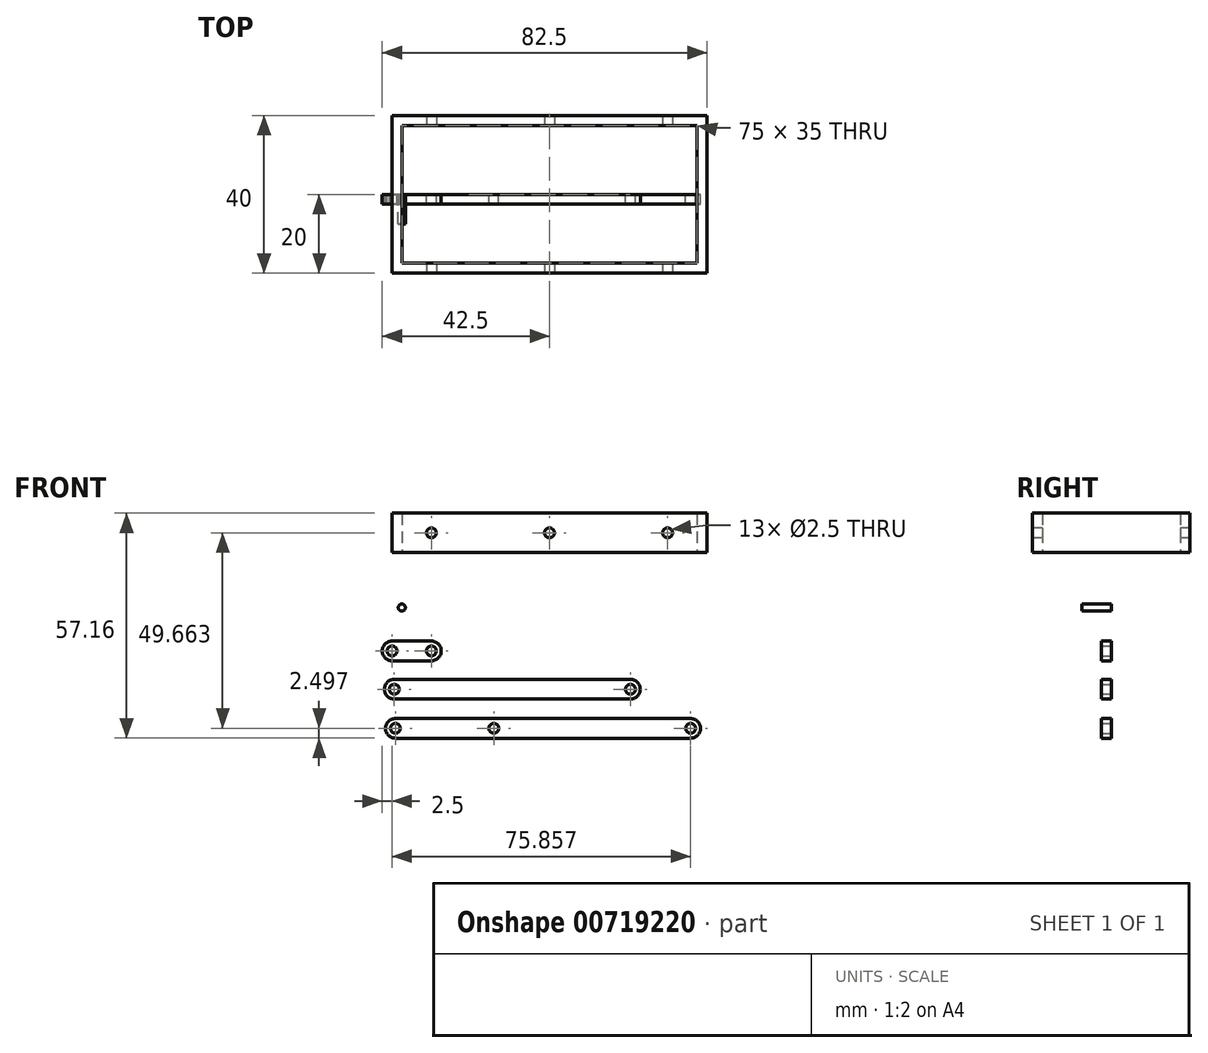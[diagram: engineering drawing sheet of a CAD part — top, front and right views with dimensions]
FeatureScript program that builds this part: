
annotation { "Feature Type Name" : "Feature", "Feature Type Description" : "" }
export const myFeature = defineFeature(function(context is Context, id is Id, definition is map)
    precondition{}
    {
        {
            assignVariable(context, id + "F0", {"name" : "thickness", "anyValue" : 2.5});
        }
        {
            var Q0;
            Q0=qCreatedBy(makeId("Front.planeOp"),FACE);
            var sketch = newSketch(context, id + "F1", { "sketchPlane" : qUnion([Q0])});
            skArc(sketch, "E0", {"start": v(0, 2.5) * mm, "mid": v(-2.5, 0) * mm, "end": v(0, -2.5) * mm});
            skArc(sketch, "E1", {"start": v(10, -2.5) * mm, "mid": v(12.5, 0) * mm, "end": v(10, 2.5) * mm});
            skLineSegment(sketch, "E2", {"start": v(0, 2.5) * mm, "end": v(10, 2.5) * mm});
            skLineSegment(sketch, "E3", {"start": v(0, -2.5) * mm, "end": v(10, -2.5) * mm});
            skCircle(sketch, "E4", {"center": v(0, 0) * mm, "radius": 1.25 * mm});
            skCircle(sketch, "E5", {"center": v(10, 0) * mm, "radius": 1.25 * mm});
            skSolve(sketch);
        }
        {
            var Q0;
            Q0=makeQuery(id+"F1.imprint","IMPRINT",FACE,{"disambiguationData":[TD([[makeQuery(id+"F1.imprint","IMPRINT",EDGE,{"derivedFrom":sQuery(id+"F1.wireOp",EDGE,"E0")}),1.0]])]});
            extrude(context, id + "F2", {"entities" : qUnion([Q0]), "depth" : (getVariable(context, 'thickness')) * mm, "offsetDistance" : 25 * mm});
        }
        {
            var Q0;
            Q0=qCreatedBy(makeId("Front.planeOp"),FACE);
            var sketch = newSketch(context, id + "F3", { "sketchPlane" : qUnion([Q0])});
            skArc(sketch, "E6", {"start": v(0.57, -7.23) * mm, "mid": v(-1.93, -9.73) * mm, "end": v(0.57, -12.23) * mm});
            skArc(sketch, "E7", {"start": v(60.57, -12.23) * mm, "mid": v(63.07, -9.73) * mm, "end": v(60.57, -7.23) * mm});
            skLineSegment(sketch, "E8", {"start": v(0.57, -7.23) * mm, "end": v(60.57, -7.23) * mm});
            skLineSegment(sketch, "E9", {"start": v(0.57, -12.23) * mm, "end": v(60.57, -12.23) * mm});
            skCircle(sketch, "E10", {"center": v(0.57, -9.73) * mm, "radius": 1.25 * mm});
            skCircle(sketch, "E11", {"center": v(60.57, -9.73) * mm, "radius": 1.25 * mm});
            skSolve(sketch);
        }
        {
            var Q0;
            Q0=makeQuery(id+"F3.imprint","IMPRINT",FACE,{"disambiguationData":[TD([[makeQuery(id+"F3.imprint","IMPRINT",EDGE,{"derivedFrom":sQuery(id+"F3.wireOp",EDGE,"E6")}),1.0]])]});
            extrude(context, id + "F4", {"entities" : qUnion([Q0]), "depth" : (getVariable(context, 'thickness')) * mm, "offsetDistance" : 25 * mm});
        }
        {
            var Q0;
            Q0=qCreatedBy(makeId("Front.planeOp"),FACE);
            var sketch = newSketch(context, id + "F5", { "sketchPlane" : qUnion([Q0])});
            skArc(sketch, "E12", {"start": v(0.86, -17.16) * mm, "mid": v(-1.64, -19.66) * mm, "end": v(0.86, -22.16) * mm});
            skArc(sketch, "E13", {"start": v(75.86, -22.16) * mm, "mid": v(78.36, -19.66) * mm, "end": v(75.86, -17.16) * mm});
            skLineSegment(sketch, "E14", {"start": v(0.86, -17.16) * mm, "end": v(75.86, -17.16) * mm});
            skLineSegment(sketch, "E15", {"start": v(0.86, -22.16) * mm, "end": v(75.86, -22.16) * mm});
            skCircle(sketch, "E16", {"center": v(0.86, -19.66) * mm, "radius": 1.25 * mm});
            skCircle(sketch, "E17", {"center": v(75.86, -19.66) * mm, "radius": 1.25 * mm});
            skCircle(sketch, "E18", {"center": v(25.86, -19.66) * mm, "radius": 1.25 * mm});
            skSolve(sketch);
        }
        {
            var Q0;
            Q0=makeQuery(id+"F5.imprint","IMPRINT",FACE,{"disambiguationData":[TD([[makeQuery(id+"F5.imprint","IMPRINT",EDGE,{"derivedFrom":sQuery(id+"F5.wireOp",EDGE,"E12")}),1.0]])]});
            extrude(context, id + "F6", {"entities" : qUnion([Q0]), "depth" : (getVariable(context, 'thickness')) * mm, "offsetDistance" : 25 * mm});
        }
        {
            var Q0;
            Q0=qCreatedBy(makeId("Top.planeOp"),FACE);
            cPlane(context, id + "F7", {"entities" : qUnion([Q0]), "cplaneType" : CPlaneType.OFFSET, "offset" : 25 * mm, "width" : 150 * mm, "height" : 150 * mm});
        }
        {
            var Q0;
            Q0=qCreatedBy(id+"F7.planeOp",FACE);
            var sketch = newSketch(context, id + "F8", { "sketchPlane" : qUnion([Q0])});
            skLineSegment(sketch, "E19.bottom", {"start": v(0, 20) * mm, "end": v(80, 20) * mm});
            skLineSegment(sketch, "E19.top", {"start": v(0, -20) * mm, "end": v(80, -20) * mm});
            skLineSegment(sketch, "E19.left", {"start": v(0, 20) * mm, "end": v(0, -20) * mm});
            skLineSegment(sketch, "E19.right", {"start": v(80, 20) * mm, "end": v(80, -20) * mm});
            skLineSegment(sketch, "E20.0", {"start": v(2.5, 17.5) * mm, "end": v(77.5, 17.5) * mm});
            skLineSegment(sketch, "E20.1", {"start": v(2.5, 17.5) * mm, "end": v(2.5, -17.5) * mm});
            skLineSegment(sketch, "E20.2", {"start": v(2.5, -17.5) * mm, "end": v(77.5, -17.5) * mm});
            skLineSegment(sketch, "E20.3", {"start": v(77.5, 17.5) * mm, "end": v(77.5, -17.5) * mm});
            skSolve(sketch);
        }
        {
            var Q0;
            Q0=makeQuery(id+"F8.imprint","IMPRINT",FACE,{"disambiguationData":[TD([[makeQuery(id+"F8.imprint","IMPRINT",EDGE,{"derivedFrom":sQuery(id+"F8.wireOp",EDGE,"E19.bottom")}),-1.0]])]});
            extrude(context, id + "F9", {"entities" : qUnion([Q0]), "depth" : 10 * mm, "offsetDistance" : 25 * mm});
        }
        {
            var Q0;
            Q0=makeQuery(id+"F9.opExtrude","SWEPT_FACE",FACE,{"disambiguationData":[OSD([sQuery(id+"F8.wireOp",EDGE,"E19.top")])]});
            var sketch = newSketch(context, id + "F10", { "sketchPlane" : qUnion([Q0])});
            skCircle(sketch, "E21", {"center": v(10, 30) * mm, "radius": 1.25 * mm});
            skCircle(sketch, "E22", {"center": v(70, 30) * mm, "radius": 1.25 * mm});
            skCircle(sketch, "E23", {"center": v(40, 30) * mm, "radius": 1.25 * mm});
            skPoint(sketch, "E23.centerSnap0", {"position": v(40, 25) * mm});
            skSolve(sketch);
        }
        {
            var Q0;
            Q0 = qSketchRegion(id + "F10", true);
            extrude(context, id + "F11", {"entities" : qUnion([Q0]), "operationType" : NewBodyOperationType.REMOVE, "endBound" : BoundingType.THROUGH_ALL, "oppositeDirection" : true, "depth" : 25 * mm, "offsetDistance" : 25 * mm});
        }
        {
            var Q0;
            Q0=qCreatedBy(makeId("Front.planeOp"),FACE);
            var sketch = newSketch(context, id + "F12", { "sketchPlane" : qUnion([Q0])});
            skCircle(sketch, "E24", {"center": v(2.49, 11.02) * mm, "radius": 0.9 * mm});
            skSolve(sketch);
        }
        {
            var Q0;
            Q0=makeQuery(id+"F12.imprint","IMPRINT",FACE,{"disambiguationData":[TD([[makeQuery(id+"F12.imprint","IMPRINT",EDGE,{"derivedFrom":sQuery(id+"F12.wireOp",EDGE,"E24")}),1.0]])]});
            extrude(context, id + "F13", {"entities" : qUnion([Q0]), "depth" : (getVariable(context, 'thickness') * 3) * mm, "offsetDistance" : 25 * mm});
        }
    });
